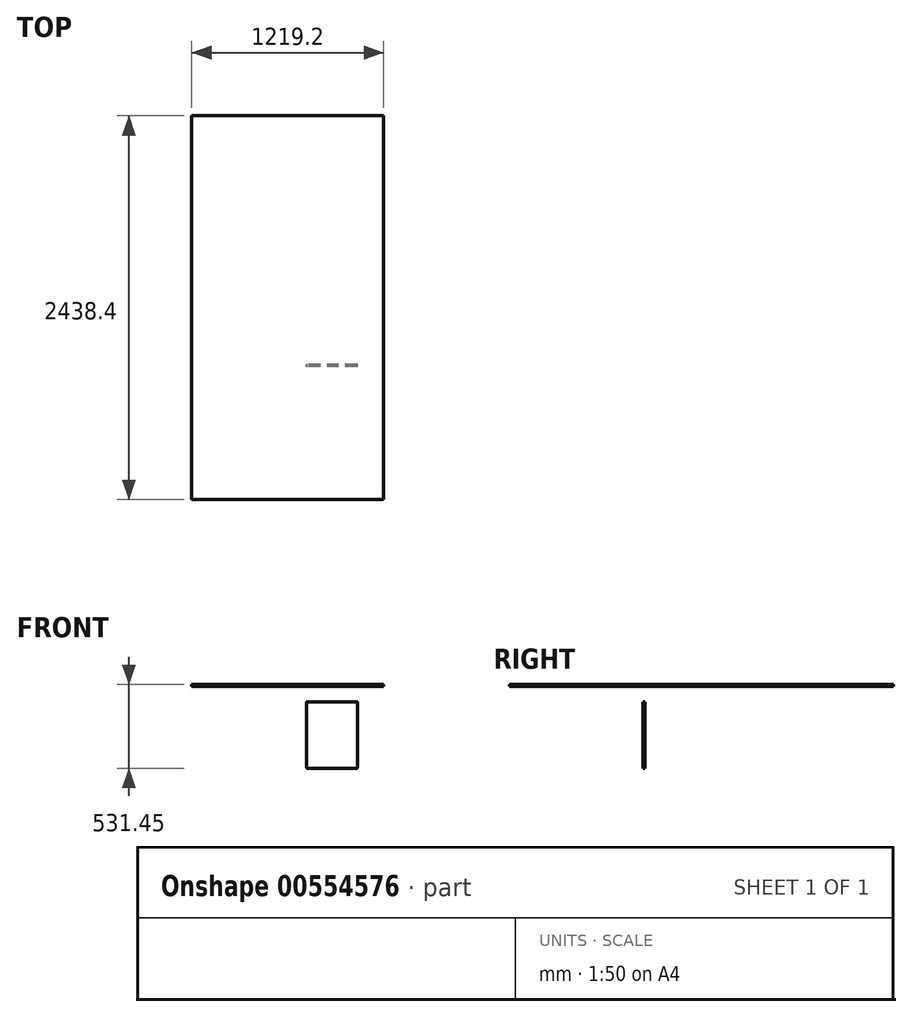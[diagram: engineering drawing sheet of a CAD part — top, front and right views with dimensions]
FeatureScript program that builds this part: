
annotation { "Feature Type Name" : "Feature", "Feature Type Description" : "" }
export const myFeature = defineFeature(function(context is Context, id is Id, definition is map)
    precondition{}
    {
        {
            var Q0;
            Q0=qCreatedBy(makeId("Top.planeOp"),FACE);
            var sketch = newSketch(context, id + "F0", { "sketchPlane" : qUnion([Q0])});
            skLineSegment(sketch, "E0.bottom", {"start": v(-631.4, 1580.77) * mm, "end": v(587.8, 1580.77) * mm});
            skLineSegment(sketch, "E0.top", {"start": v(-631.4, -857.63) * mm, "end": v(587.8, -857.63) * mm});
            skLineSegment(sketch, "E0.left", {"start": v(-631.4, 1580.77) * mm, "end": v(-631.4, -857.63) * mm});
            skLineSegment(sketch, "E0.right", {"start": v(587.8, 1580.77) * mm, "end": v(587.8, -857.63) * mm});
            skSolve(sketch);
        }
        {
            var Q0;
            Q0 = qSketchRegion(id + "F0", true);
            extrude(context, id + "F1", {"entities" : qUnion([Q0]), "depth" : 12.7 * mm, "offsetDistance" : 25.4 * mm});
        }
        {
            var Q0;
            Q0=qCreatedBy(makeId("Front.planeOp"),FACE);
            var sketch = newSketch(context, id + "F2", { "sketchPlane" : qUnion([Q0])});
            skLineSegment(sketch, "E1.bottom", {"start": v(421.28, -518.75) * mm, "end": v(97.43, -518.75) * mm});
            skLineSegment(sketch, "E1.top", {"start": v(421.28, -96.48) * mm, "end": v(97.43, -96.48) * mm});
            skLineSegment(sketch, "E1.left", {"start": v(421.28, -518.75) * mm, "end": v(421.28, -96.48) * mm});
            skLineSegment(sketch, "E1.right", {"start": v(97.43, -518.75) * mm, "end": v(97.43, -96.48) * mm});
            skSolve(sketch);
        }
        {
            var Q0;
            Q0 = qSketchRegion(id + "F2", true);
            extrude(context, id + "F3", {"entities" : qUnion([Q0]), "depth" : 12.7 * mm, "offsetDistance" : 25.4 * mm});
        }
        {
            var Q0;
            Q0=makeQuery(id+"F3.opExtrude","SWEPT_EDGE",EDGE,{"disambiguationData":[OSD([sQuery(id+"F2.wireOp",EDGE,"E1.bottom"),sQuery(id+"F2.wireOp",EDGE,"E1.left")])]});
            var Q1;
            Q1=makeQuery(id+"F3.opExtrude","SWEPT_EDGE",EDGE,{"disambiguationData":[OSD([sQuery(id+"F2.wireOp",EDGE,"E1.bottom"),sQuery(id+"F2.wireOp",EDGE,"E1.right")])]});
            var Q2;
            Q2=makeQuery(id+"F3.opExtrude","SWEPT_EDGE",EDGE,{"disambiguationData":[OSD([sQuery(id+"F2.wireOp",EDGE,"E1.top"),sQuery(id+"F2.wireOp",EDGE,"E1.right")])]});
            var Q3;
            Q3=makeQuery(id+"F3.opExtrude","SWEPT_EDGE",EDGE,{"disambiguationData":[OSD([sQuery(id+"F2.wireOp",EDGE,"E1.top"),sQuery(id+"F2.wireOp",EDGE,"E1.left")])]});
            fillet(context, id + "F4", {"entities" : qUnion([Q0, Q1, Q2, Q3]), "radius" : 5.08 * mm, "tangentPropagation" : true, "allowEdgeOverflow" : false});
        }
    });
